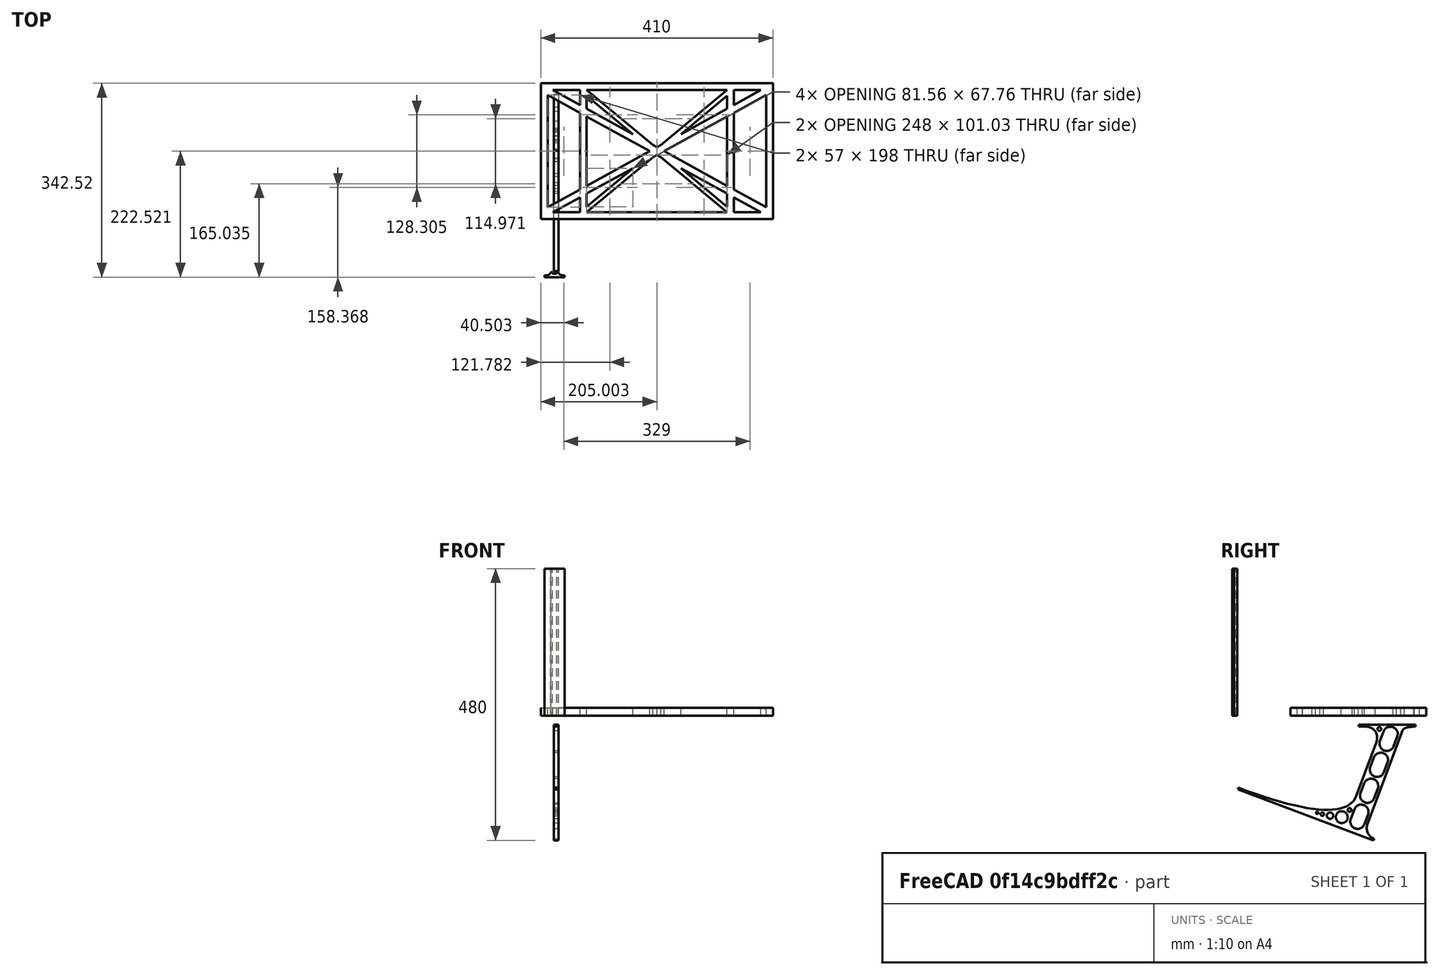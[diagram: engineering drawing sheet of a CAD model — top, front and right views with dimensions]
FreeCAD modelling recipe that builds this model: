
FCSTD DOCUMENT  (FreeCAD 0.19R0.19.2)
Label: laptopStand046
License: All rights reserved
LicenseURL: http://en.wikipedia.org/wiki/All_rights_reserved
objects: Sketcher::SketchObject×3, Part::Extrusion×3
note: 6 computed .brp shape members not serialized (recipe doc carries the construction recipe); baked Part::Feature solids carry a one-line shape summary decoded from their .brp

FEATURE [Sketcher::SketchObject] Sketch
  FullyConstrained = false
  sketch-geometry (66):
    g0: LineSegment StartX=-22.9272 StartY=136.221 StartZ=0 EndX=387.073 EndY=136.221 EndZ=0
    g1: LineSegment StartX=-22.9272 StartY=-103.779 StartZ=0 EndX=387.073 EndY=-103.779 EndZ=0
    g2: LineSegment StartX=375.073 StartY=115.221 StartZ=0 EndX=318.073 EndY=83.9235 EndZ=0
    g3: LineSegment StartX=-10.9272 StartY=-82.7794 StartZ=0 EndX=46.0728 EndY=-51.4823 EndZ=0
    g4: LineSegment StartX=-1.92719 StartY=124.221 StartZ=0 EndX=46.0728 EndY=97.8651 EndZ=0
    g5: LineSegment StartX=366.073 StartY=-91.7794 StartZ=0 EndX=318.073 EndY=-65.424 EndZ=0
    g6: LineSegment StartX=-10.9272 StartY=115.221 StartZ=0 EndX=-10.9272 EndY=-82.7794 EndZ=0
    g7: LineSegment StartX=375.073 StartY=-82.7794 StartZ=0 EndX=375.073 EndY=115.221 EndZ=0
    g8: LineSegment StartX=-1.92719 StartY=-91.7794 StartZ=0 EndX=46.0728 EndY=-91.7794 EndZ=0
    g9: LineSegment StartX=318.073 StartY=124.221 StartZ=0 EndX=366.073 EndY=124.221 EndZ=0
    g10: LineSegment StartX=306.073 StartY=-81.8102 StartZ=0 EndX=224.513 EndY=-14.0532 EndZ=0
    g11: LineSegment StartX=58.0728 StartY=114.251 StartZ=0 EndX=139.632 EndY=46.4944 EndZ=0
    g12: LineSegment StartX=306.073 StartY=124.221 StartZ=0 EndX=189.124 EndY=27.0628 EndZ=0
    g13: LineSegment StartX=58.0728 StartY=-91.7794 StartZ=0 EndX=175.022 EndY=5.37834 EndZ=0
    g14: LineSegment StartX=46.0728 StartY=124.221 StartZ=0 EndX=46.0728 EndY=97.8651 EndZ=0
    g15: LineSegment StartX=58.0728 StartY=-81.8102 StartZ=0 EndX=58.0728 EndY=-58.8351 EndZ=0
    g16: LineSegment StartX=318.073 StartY=124.221 StartZ=0 EndX=318.073 EndY=97.8651 EndZ=0
    g17: LineSegment StartX=306.073 StartY=114.251 StartZ=0 EndX=306.073 EndY=91.2763 EndZ=0
    g18: LineSegment StartX=224.513 StartY=46.4944 StartZ=0 EndX=306.073 EndY=114.251 EndZ=0
    g19: LineSegment StartX=175.022 StartY=27.0628 StartZ=0 EndX=58.0728 EndY=124.221 EndZ=0
    g20: LineSegment StartX=169.377 StartY=16.2206 StartZ=0 EndX=58.0728 EndY=77.3346 EndZ=0
    g21: LineSegment StartX=139.632 StartY=-14.0532 StartZ=0 EndX=58.0728 EndY=-81.8102 EndZ=0
    g22: LineSegment StartX=194.768 StartY=16.2206 StartZ=0 EndX=306.073 EndY=-44.8935 EndZ=0
    g23: LineSegment StartX=224.513 StartY=46.4944 StartZ=0 EndX=306.073 EndY=91.2763 EndZ=0
    g24: LineSegment StartX=175.022 StartY=27.0628 StartZ=0 EndX=179.022 EndY=24.8665 EndZ=0
    g25: LineSegment StartX=139.632 StartY=-14.0532 StartZ=0 EndX=58.0728 EndY=-58.8351 EndZ=0
    g26: LineSegment StartX=189.124 StartY=5.37834 StartZ=0 EndX=185.124 EndY=7.57463 EndZ=0
    g27: LineSegment StartX=189.124 StartY=5.37834 StartZ=0 EndX=306.073 EndY=-91.7794 EndZ=0
    g28: LineSegment StartX=306.073 StartY=77.3346 StartZ=0 EndX=306.073 EndY=-44.8935 EndZ=0
    g29: LineSegment StartX=318.073 StartY=83.9235 StartZ=0 EndX=318.073 EndY=-51.4823 EndZ=0
    g30: LineSegment StartX=318.073 StartY=97.8651 StartZ=0 EndX=366.073 EndY=124.221 EndZ=0
    g31: LineSegment StartX=306.073 StartY=77.3346 StartZ=0 EndX=194.768 EndY=16.2206 EndZ=0
    g32: LineSegment StartX=306.073 StartY=-58.8351 StartZ=0 EndX=224.513 EndY=-14.0532 EndZ=0
    g33: LineSegment StartX=306.073 StartY=-58.8351 StartZ=0 EndX=306.073 EndY=-81.8102 EndZ=0
    g34: LineSegment StartX=318.073 StartY=-51.4823 StartZ=0 EndX=375.073 EndY=-82.7794 EndZ=0
    g35: LineSegment StartX=318.073 StartY=-65.424 StartZ=0 EndX=318.073 EndY=-91.7794 EndZ=0
    g36: LineSegment StartX=306.073 StartY=124.221 StartZ=0 EndX=58.0728 EndY=124.221 EndZ=0
    g37: LineSegment StartX=318.073 StartY=-91.7794 StartZ=0 EndX=366.073 EndY=-91.7794 EndZ=0
    g38: LineSegment StartX=58.0728 StartY=-91.7794 StartZ=0 EndX=306.073 EndY=-91.7794 EndZ=0
    g39: LineSegment StartX=58.0728 StartY=-44.8935 StartZ=0 EndX=58.0728 EndY=77.3346 EndZ=0
    g40: LineSegment StartX=46.0728 StartY=-65.424 StartZ=0 EndX=-1.92719 EndY=-91.7794 EndZ=0
    g41: LineSegment StartX=46.0728 StartY=-65.424 StartZ=0 EndX=46.0728 EndY=-91.7794 EndZ=0
    g42: LineSegment StartX=58.0728 StartY=-44.8935 StartZ=0 EndX=169.377 EndY=16.2206 EndZ=0
    g43: LineSegment StartX=58.0728 StartY=91.2763 StartZ=0 EndX=58.0728 EndY=114.251 EndZ=0
    g44: LineSegment StartX=46.0728 StartY=83.9235 StartZ=0 EndX=46.0728 EndY=-51.4823 EndZ=0
    g45: LineSegment StartX=46.0728 StartY=124.221 StartZ=0 EndX=-1.92719 EndY=124.221 EndZ=0
    g46: LineSegment StartX=58.0728 StartY=91.2763 StartZ=0 EndX=139.632 EndY=46.4944 EndZ=0
    g47: LineSegment StartX=46.0728 StartY=83.9235 StartZ=0 EndX=-10.9272 EndY=115.221 EndZ=0
    g48: LineSegment StartX=-22.9272 StartY=136.221 StartZ=0 EndX=-42.9272 EndY=136.221 EndZ=0
    g49: LineSegment StartX=387.073 StartY=136.221 StartZ=0 EndX=407.073 EndY=136.221 EndZ=0
    g50: LineSegment StartX=-42.9272 StartY=136.221 StartZ=0 EndX=-42.9272 EndY=-103.779 EndZ=0
    g51: LineSegment StartX=-22.9272 StartY=-103.779 StartZ=0 EndX=-42.9272 EndY=-103.779 EndZ=0
    g52: LineSegment StartX=407.073 StartY=136.221 StartZ=0 EndX=407.073 EndY=-103.779 EndZ=0
    g53: LineSegment StartX=387.073 StartY=-103.779 StartZ=0 EndX=407.073 EndY=-103.779 EndZ=0
    g54: LineSegment StartX=179.022 StartY=27.0628 StartZ=0 EndX=179.022 EndY=124.221 EndZ=0
    g55: LineSegment StartX=185.124 StartY=27.0628 StartZ=0 EndX=185.124 EndY=124.221 EndZ=0
    g56: LineSegment StartX=179.022 StartY=27.0628 StartZ=0 EndX=179.022 EndY=24.8665 EndZ=0
    g57: LineSegment StartX=185.124 StartY=27.0628 StartZ=0 EndX=185.124 EndY=24.8665 EndZ=0
    g58: LineSegment StartX=185.124 StartY=7.57463 StartZ=0 EndX=185.124 EndY=-91.7794 EndZ=0
    g59: LineSegment StartX=179.022 StartY=7.57463 StartZ=0 EndX=179.022 EndY=-91.7794 EndZ=0
    g60: LineSegment StartX=189.124 StartY=27.0628 StartZ=0 EndX=185.124 EndY=24.8665 EndZ=0
    g61: LineSegment StartX=175.022 StartY=5.37834 StartZ=0 EndX=179.022 EndY=7.57463 EndZ=0
    g62: ArcOfCircle CenterX=-26.9272 CenterY=22.1087 CenterZ=0 NormalX=0 NormalY=0 NormalZ=1 AngleXU=0 Radius=8 StartAngle=1e-16 EndAngle=3.14159
    g63: ArcOfCircle CenterX=-26.9272 CenterY=-83.7794 CenterZ=0 NormalX=0 NormalY=0 NormalZ=1 AngleXU=0 Radius=8 StartAngle=3.14159 EndAngle=6.28319
    g64: LineSegment StartX=-34.9272 StartY=22.1087 StartZ=0 EndX=-34.9272 EndY=-83.7794 EndZ=0
    g65: LineSegment StartX=-18.9272 StartY=22.1087 StartZ=0 EndX=-18.9272 EndY=-83.7794 EndZ=0
  constraints (132):
    c: Horizontal(g0)
    c: Distance(g0) = 410
    c: Horizontal(g1)
    c: Block(g0)
    c: Horizontal(g8)
    c: Horizontal(g9)
    c: Tangent(g5,g20)
    c: PointOnObject(g20,g3)
    c: PointOnObject(g22,g2)
    c: Coincident(g46,g11)
    c: Coincident(g24,g19)
    c: Coincident(g18,g23)
    c: Coincident(g25,g21)
    c: Coincident(g32,g10)
    c: Coincident(g27,g26)
    c: Coincident(g18,g17)
    c: Tangent(g17,g28)
    c: Tangent(g16,g29)
    c: Coincident(g23,g17)
    c: Tangent(g23,g30)
    c: Coincident(g2,g29)
    c: Coincident(g31,g28)
    c: Tangent(g2,g31)
    c: Coincident(g33,g10)
    c: Tangent(g5,g32)
    c: Tangent(g28,g33)
    c: Coincident(g22,g28)
    c: Tangent(g22,g34)
    c: Coincident(g29,g34)
    c: Coincident(g35,g5)
    c: Tangent(g29,g35)
    c: Coincident(g21,g15)
    c: Tangent(g15,g39)
    c: Coincident(g25,g15)
    c: Tangent(g25,g40)
    c: Coincident(g41,g40)
    c: Tangent(g14,g41)
    c: Coincident(g3,g44)
    c: Coincident(g42,g39)
    c: Tangent(g3,g42)
    c: Tangent(g39,g43)
    c: Tangent(g14,g44)
    c: Coincident(g11,g43)
    c: PointOnObject(g36,g19)
    c: Tangent(g36,g45)
    c: Coincident(g4,g14)
    c: Coincident(g46,g43)
    c: Tangent(g4,g46)
    c: Coincident(g20,g39)
    c: Coincident(g47,g44)
    c: Tangent(g20,g47)
    c: Block(g19)
    c: Block(g12)
    c: Block(g36)
    c: Block(g16)
    c: Block(g30)
    c: Block(g2)
    c: Block(g34)
    c: Block(g7)
    c: Block(g32)
    c: Block(g33)
    c: Block(g5)
    c: Block(g35)
    c: Block(g18)
    c: Block(g27)
    c: Block(g38)
    c: Block(g13)
    c: Block(g25)
    c: Block(g21)
    c: Block(g41)
    c: Block(g40)
    c: Block(g3)
    c: Block(g6)
    c: Block(g47)
    c: Block(g4)
    c: Block(g14)
    c: Block(g11)
    c: Block(g43)
    c: Block(g31)
    c: Block(g28)
    c: Block(g20)
    c: Block(g42)
    c: Block(g45)
    c: Block(g9)
    c: Block(g37)
    c: Block(g8)
    c: Horizontal(g48)
    c: Distance(g48) = 20
    c: Coincident(g49,g0)
    c: Horizontal(g49)
    c: Distance(g49) = 20
    c: Coincident(g50,g48)
    c: Vertical(g50)
    c: Horizontal(g51)
    c: Coincident(g51,g50)
    c: Coincident(g52,g49)
    c: Vertical(g52)
    c: Coincident(g53,g1)
    c: Horizontal(g53)
    c: Coincident(g53,g52)
    c: Block(g52)
    c: Block(g51)
    c: Block(g50)
    c: Block(g1)
    c: Vertical(g54)
    c: Vertical(g55)
    c: Vertical(g56)
    c: Vertical(g57)
    c: PointOnObject(g55,g36)
    c: PointOnObject(g54,g36)
    c: Tangent(g57,g58)
    c: PointOnObject(g58,g38)
    c: PointOnObject(g59,g38)
    c: Tangent(g56,g59)
    c: Coincident(g24,g56)
    c: Coincident(g26,g58)
    c: Block(g54)
    c: Block(g55)
    c: Block(g59)
    c: Block(g58)
    c: Coincident(g60,g12)
    c: Coincident(g60,g57)
    c: Coincident(g61,g13)
    c: Coincident(g61,g59)
    c: Tangent(g62,g65) = 1.5708
    c: Tangent(g62,g64) = -1.5708
    c: Tangent(g64,g63) = -1.5708
    c: Tangent(g65,g63) = 1.5708
    c: Vertical(g64)
    c: Equal(g62,g63)
    c: Block(g65)
    c: Block(g64)
FEATURE [Sketcher::SketchObject] Sketch001
  FullyConstrained = true
  MapMode = 4
  Placement = pos=(0,0,0) rot=(0.57735,0.57735,0.57735;2.0944rad)
  Support = -> [Sketch]
  sketch-geometry (46):
    g0: BSplineCurve PolesCount=3 KnotsCount=2 Degree=2 IsPeriodic=0
    g1: ArcOfCircle CenterX=73.122 CenterY=-32.2909 CenterZ=0 NormalX=0 NormalY=0 NormalZ=1 AngleXU=0 Radius=13 StartAngle=5.92268 EndAngle=9.06428
    g2: ArcOfCircle CenterX=66.7816 CenterY=-49.1439 CenterZ=0 NormalX=0 NormalY=0 NormalZ=1 AngleXU=0 Radius=13 StartAngle=2.78068 EndAngle=5.92131
    g3: ArcOfCircle CenterX=55.9263 CenterY=-78.1807 CenterZ=0 NormalX=0 NormalY=0 NormalZ=1 AngleXU=0 Radius=13 StartAngle=5.92268 EndAngle=9.06428
    g4: ArcOfCircle CenterX=49.5884 CenterY=-95.0342 CenterZ=0 NormalX=0 NormalY=0 NormalZ=1 AngleXU=0 Radius=13 StartAngle=2.78068 EndAngle=5.92131
    g5: ArcOfCircle CenterX=38.7206 CenterY=-124.067 CenterZ=0 NormalX=0 NormalY=0 NormalZ=1 AngleXU=0 Radius=13 StartAngle=5.92268 EndAngle=9.06428
    g6: ArcOfCircle CenterX=32.3875 CenterY=-140.92 CenterZ=0 NormalX=0 NormalY=0 NormalZ=1 AngleXU=0 Radius=13 StartAngle=2.78068 EndAngle=5.92131
    g7: ArcOfCircle CenterX=21.4715 CenterY=-169.934 CenterZ=0 NormalX=0 NormalY=0 NormalZ=1 AngleXU=0 Radius=13 StartAngle=5.92268 EndAngle=9.06428
    g8: ArcOfCircle CenterX=15.1336 CenterY=-186.787 CenterZ=0 NormalX=0 NormalY=0 NormalZ=1 AngleXU=0 Radius=13 StartAngle=2.78068 EndAngle=5.92131
    g9-g12: Circle x4 (B-spline internal-alignment scaffolding for g13; pole/knot coordinates omitted)
    g13: BSplineCurve PolesCount=4 KnotsCount=2 Degree=3 IsPeriodic=0
    g14: GeomPoint X=28.8094 Y=-19.0875 Z=0
    g15: GeomPoint X=47.0443 Y=-50.4712 Z=0
    g16: Circle CenterX=53.5586 CenterY=-23.2695 CenterZ=0 NormalX=0 NormalY=0 NormalZ=1 AngleXU=0 Radius=3.24518
    g17: Circle CenterX=-195.441 CenterY=-127.082 CenterZ=0 NormalX=0 NormalY=0 NormalZ=1 AngleXU=0 Radius=1
    g18: Circle CenterX=-8.24091 CenterY=-197.481 CenterZ=0 NormalX=0 NormalY=0 NormalZ=1 AngleXU=0 Radius=1
    g19: Circle CenterX=12.8789 CenterY=-141.321 CenterZ=0 NormalX=0 NormalY=0 NormalZ=1 AngleXU=0 Radius=1
    g20: BSplineCurve PolesCount=3 KnotsCount=2 Degree=2 IsPeriodic=0
    g21: GeomPoint X=-195.441 Y=-127.082 Z=0
    g22: GeomPoint X=12.8789 Y=-141.321 Z=0
    g23: Circle CenterX=-12.8016 CenterY=-179.036 CenterZ=0 NormalX=0 NormalY=0 NormalZ=1 AngleXU=0 Radius=10.5072
    g24: Circle CenterX=0.933922 CenterY=-166.43 CenterZ=0 NormalX=0 NormalY=0 NormalZ=1 AngleXU=0 Radius=3.26661
    g25: Circle CenterX=-33.5518 CenterY=-176.44 CenterZ=0 NormalX=0 NormalY=0 NormalZ=1 AngleXU=0 Radius=5.64388
    g26: Circle CenterX=-47.2366 CenterY=-173.859 CenterZ=0 NormalX=0 NormalY=0 NormalZ=1 AngleXU=0 Radius=3.01653
    g27: Circle CenterX=-56.2595 CenterY=-171.456 CenterZ=0 NormalX=0 NormalY=0 NormalZ=1 AngleXU=0 Radius=2.12826
    g28: ArcOfCircle CenterX=51.2151 CenterY=-198.473 CenterZ=0 NormalX=0 NormalY=0 NormalZ=1 AngleXU=0 Radius=20 StartAngle=2.78189 EndAngle=4.35269
    g29: LineSegment StartX=32.4951 StartY=-191.433 StartZ=0 EndX=94.6577 EndY=-26.1351 EndZ=0
    g30: LineSegment StartX=43.1192 StartY=-220.001 StartZ=0 EndX=-196.497 EndY=-129.89 EndZ=0
    g31: LineSegment StartX=43.1192 StartY=-220.001 StartZ=0 EndX=44.1752 EndY=-217.193 EndZ=0
    g32: LineSegment StartX=117.223 StartY=-19.0875 StartZ=0 EndX=117.223 EndY=-16.0875 EndZ=0
    g33: LineSegment StartX=117.223 StartY=-16.0875 StartZ=0 EndX=17.2232 EndY=-16.0875 EndZ=0
    g34: LineSegment StartX=17.2232 StartY=-16.0875 StartZ=0 EndX=17.2232 EndY=-19.0875 EndZ=0
    g35: LineSegment StartX=28.8094 StartY=-19.0875 StartZ=0 EndX=17.2232 EndY=-19.0875 EndZ=0
    g36: LineSegment StartX=47.0443 StartY=-50.4712 StartZ=0 EndX=12.8789 EndY=-141.321 EndZ=0
    g37: LineSegment StartX=-195.441 StartY=-127.082 StartZ=0 EndX=-196.497 EndY=-129.89 EndZ=0
    g38: LineSegment StartX=85.2864 StartY=-36.8765 StartZ=0 EndX=78.9396 EndY=-53.7463 EndZ=0
    g39: LineSegment StartX=60.9577 StartY=-27.7052 StartZ=0 EndX=54.6191 EndY=-44.5532 EndZ=0
    g40: LineSegment StartX=68.0907 StartY=-82.7664 StartZ=0 EndX=61.7465 EndY=-99.6365 EndZ=0
    g41: LineSegment StartX=43.7619 StartY=-73.595 StartZ=0 EndX=37.426 EndY=-90.4435 EndZ=0
    g42: LineSegment StartX=50.885 StartY=-128.652 StartZ=0 EndX=44.5456 EndY=-145.522 EndZ=0
    g43: LineSegment StartX=26.5562 StartY=-119.481 StartZ=0 EndX=20.2251 EndY=-136.329 EndZ=0
    g44: LineSegment StartX=9.3071 StartY=-165.349 StartZ=0 EndX=2.97115 EndY=-182.197 EndZ=0
    g45: LineSegment StartX=33.6358 StartY=-174.52 StartZ=0 EndX=27.2917 EndY=-191.39 EndZ=0
  constraints (70):
    c: Block(g0)
    c: Block(g1)
    c: Block(g2)
    c: Block(g4)
    c: Block(g3)
    c: Block(g6)
    c: Block(g5)
    c: Block(g8)
    c: Block(g7)
    c: Weight(g9) = 1
    c: Equal(g9,g10)
    c: Equal(g9,g11)
    c: Equal(g9,g12)
    c: InternalAlignment(g9-g12 -> g13) x4
    c: InternalAlignment(g14,g13)
    c: InternalAlignment(g15,g13)
    c: Block(g16)
    c: Weight(g17) = 1
    c: Equal(g17,g18)
    c: Equal(g17,g19)
    c: InternalAlignment(g17,g20)
    c: InternalAlignment(g18,g20)
    c: InternalAlignment(g19,g20)
    c: InternalAlignment(g21,g20)
    c: InternalAlignment(g22,g20)
    c: Block(g20)
    c: Block(g23)
    c: Block(g24)
    c: Block(g25)
    c: Block(g26)
    c: Block(g27)
    c: Block(g28)
    c: Coincident(g29,g28)
    c: Coincident(g29,g0)
    c: Block(g13)
    c: Coincident(g31,g30)
    c: Coincident(g31,g28)
    c: Block(g31)
    c: Coincident(g32,g0)
    c: Vertical(g32)
    c: Coincident(g33,g32)
    c: Horizontal(g33)
    c: Coincident(g34,g33)
    c: Vertical(g34)
    c: Block(g33)
    c: Coincident(g35,g13)
    c: Coincident(g35,g34)
    c: Horizontal(g35)
    c: Coincident(g36,g13)
    c: Coincident(g36,g20)
    c: Coincident(g37,g20)
    c: Coincident(g37,g30)
    c: Block(g30)
    c: Coincident(g38,g1)
    c: Coincident(g38,g2)
    c: Coincident(g39,g1)
    c: Coincident(g39,g2)
    c: Coincident(g40,g3)
    c: Coincident(g40,g4)
    c: Coincident(g41,g3)
    c: Coincident(g41,g4)
    c: Coincident(g42,g5)
    c: Coincident(g42,g6)
    c: Coincident(g43,g5)
    c: Coincident(g43,g6)
    c: Coincident(g44,g7)
    c: Coincident(g44,g8)
    c: Coincident(g45,g7)
    c: Coincident(g45,g8)
    c: Distance(g30) = 256
FEATURE [Part::Extrusion] Extrude002
  Base = -> Sketch001
  Dir = (1,0,0)
  DirMode = 2
  FaceMakerClass = Part::FaceMakerBullseye
  LengthFwd = 8
  LengthRev = 0
  Solid = true
  Symmetric = false
FEATURE [Sketcher::SketchObject] Sketch002
  FullyConstrained = true
  sketch-geometry (20):
    g0: LineSegment StartX=-2.77179 StartY=-200.304 StartZ=0 EndX=5.22821 EndY=-200.304 EndZ=0
    g1: LineSegment StartX=5.22821 StartY=-200.304 StartZ=0 EndX=5.22821 EndY=-197.304 EndZ=0
    g2: LineSegment StartX=-2.77179 StartY=-200.304 StartZ=0 EndX=-2.77179 EndY=-197.304 EndZ=0
    g3: LineSegment StartX=5.22821 StartY=-197.304 StartZ=0 EndX=8.22821 EndY=-197.304 EndZ=0
    g4: LineSegment StartX=-2.77179 StartY=-197.304 StartZ=0 EndX=-5.77179 EndY=-197.304 EndZ=0
    g5: LineSegment StartX=19.2282 StartY=-203.304 StartZ=0 EndX=19.2282 EndY=-206.304 EndZ=0
    g6: LineSegment StartX=-16.7718 StartY=-203.304 StartZ=0 EndX=-16.7718 EndY=-206.304 EndZ=0
    g7: LineSegment StartX=-16.7718 StartY=-206.304 StartZ=0 EndX=19.2282 EndY=-206.304 EndZ=0
    g8: Circle CenterX=-16.7718 CenterY=-203.304 CenterZ=0 NormalX=0 NormalY=0 NormalZ=1 AngleXU=0 Radius=1
    g9: Circle CenterX=-5.77179 CenterY=-203.304 CenterZ=0 NormalX=0 NormalY=0 NormalZ=1 AngleXU=0 Radius=1
    g10: Circle CenterX=-5.77179 CenterY=-197.304 CenterZ=0 NormalX=0 NormalY=0 NormalZ=1 AngleXU=0 Radius=1
    g11: BSplineCurve PolesCount=3 KnotsCount=2 Degree=2 IsPeriodic=0
    g12: GeomPoint X=-16.7718 Y=-203.304 Z=0
    g13: GeomPoint X=-5.77179 Y=-197.304 Z=0
    g14: Circle CenterX=19.2282 CenterY=-203.304 CenterZ=0 NormalX=0 NormalY=0 NormalZ=1 AngleXU=0 Radius=1
    g15: Circle CenterX=8.22821 CenterY=-203.304 CenterZ=0 NormalX=0 NormalY=0 NormalZ=1 AngleXU=0 Radius=1
    g16: Circle CenterX=8.22821 CenterY=-197.304 CenterZ=0 NormalX=0 NormalY=0 NormalZ=1 AngleXU=0 Radius=1
    g17: BSplineCurve PolesCount=3 KnotsCount=2 Degree=2 IsPeriodic=0
    g18: GeomPoint X=19.2282 Y=-203.304 Z=0
    g19: GeomPoint X=8.22821 Y=-197.304 Z=0
  constraints (41):
    c: Horizontal(g0)
    c: Distance(g0) = 8
    c: Coincident(g1,g0)
    c: Vertical(g1)
    c: Distance(g1) = 3
    c: Coincident(g2,g0)
    c: Vertical(g2)
    c: Distance(g2) = 3
    c: Coincident(g3,g1)
    c: Horizontal(g3)
    c: Distance(g3) = 3
    c: Coincident(g4,g2)
    c: Horizontal(g4)
    c: Distance(g4) = 3
    c: Vertical(g5)
    c: Vertical(g6)
    c: Coincident(g7,g6)
    c: Coincident(g7,g5)
    c: Weight(g8) = 1
    c: Equal(g8,g9)
    c: Equal(g8,g10)
    c: Coincident(g11,g4)
    c: InternalAlignment(g8,g11)
    c: InternalAlignment(g9,g11)
    c: InternalAlignment(g10,g11)
    c: InternalAlignment(g12,g11)
    c: InternalAlignment(g13,g11)
    c: Coincident(g17,g5)
    c: Weight(g14) = 1
    c: Equal(g14,g15)
    c: Equal(g14,g16)
    c: Coincident(g17,g3)
    c: InternalAlignment(g14,g17)
    c: InternalAlignment(g15,g17)
    c: InternalAlignment(g16,g17)
    c: InternalAlignment(g18,g17)
    c: InternalAlignment(g19,g17)
    c: Block(g7)
    c: Block(g17)
    c: Block(g11)
    c: Block(g6)
FEATURE [Part::Extrusion] Extrude003
  Base = -> Sketch002
  Dir = (0,0,1)
  DirMode = 2
  FaceMakerClass = Part::FaceMakerBullseye
  LengthFwd = 260
  LengthRev = 0
  Solid = true
  Symmetric = false
FEATURE [Part::Extrusion] Extrude
  Base = -> Sketch
  Dir = (0,0,1)
  DirMode = 2
  FaceMakerClass = Part::FaceMakerBullseye
  LengthFwd = 14
  LengthRev = 0
  Solid = true
  Symmetric = false
